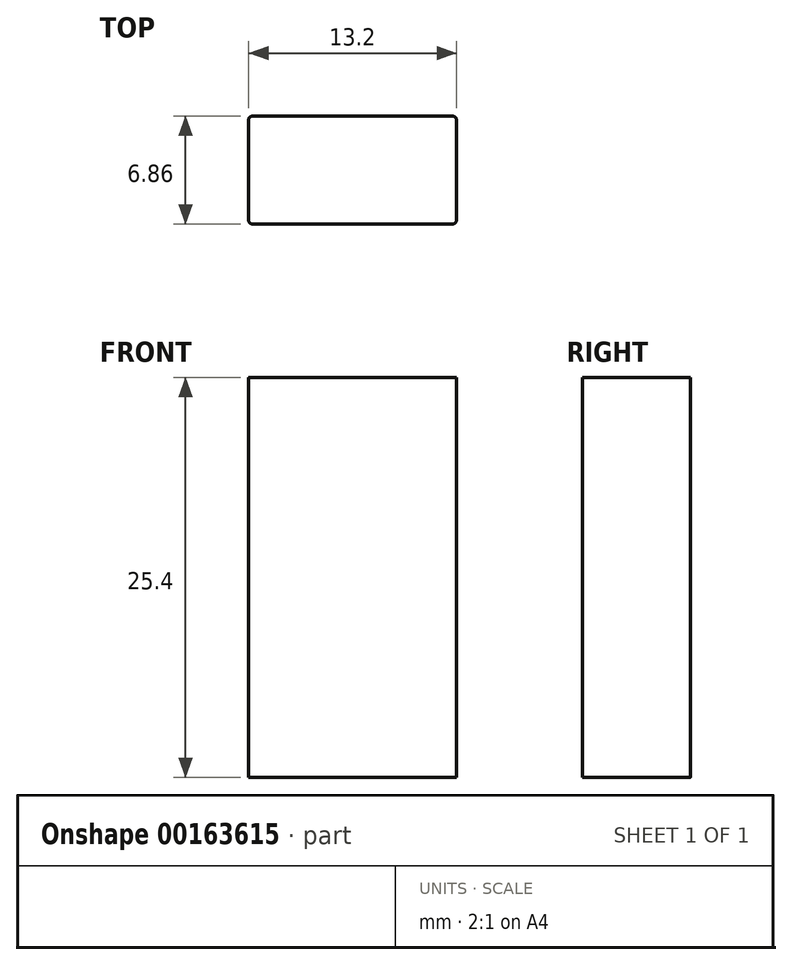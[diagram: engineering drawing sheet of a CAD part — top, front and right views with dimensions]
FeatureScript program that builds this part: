
annotation { "Feature Type Name" : "Feature", "Feature Type Description" : "" }
export const myFeature = defineFeature(function(context is Context, id is Id, definition is map)
    precondition{}
    {
        {
            var Q0;
            Q0=qCreatedBy(makeId("Top.planeOp"),FACE);
            var sketch = newSketch(context, id + "F0", { "sketchPlane" : qUnion([Q0])});
            skLineSegment(sketch, "E0.bottom", {"start": v(6.35, 3.43) * mm, "end": v(-6.35, 3.43) * mm});
            skLineSegment(sketch, "E0.top", {"start": v(6.35, -3.43) * mm, "end": v(-6.35, -3.43) * mm});
            skLineSegment(sketch, "E0.left", {"start": v(6.6, 3.18) * mm, "end": v(6.6, -3.18) * mm});
            skLineSegment(sketch, "E0.right", {"start": v(-6.6, 3.18) * mm, "end": v(-6.6, -3.17) * mm});
            skPoint(sketch, "E0.middle", {"position": v(0, 0) * mm});
            skPoint(sketch, "E1.visualSharp", {"position": v(-6.6, 3.43) * mm});
            skArc(sketch, "E1.filletArc", {"start": v(-6.35, 3.43) * mm, "mid": v(-6.53, 3.35) * mm, "end": v(-6.6, 3.18) * mm});
            skPoint(sketch, "E2.visualSharp", {"position": v(6.6, 3.43) * mm});
            skArc(sketch, "E2.filletArc", {"start": v(6.6, 3.18) * mm, "mid": v(6.53, 3.35) * mm, "end": v(6.35, 3.43) * mm});
            skPoint(sketch, "E3.visualSharp", {"position": v(6.6, -3.43) * mm});
            skArc(sketch, "E3.filletArc", {"start": v(6.35, -3.43) * mm, "mid": v(6.53, -3.35) * mm, "end": v(6.6, -3.18) * mm});
            skPoint(sketch, "E4.visualSharp", {"position": v(-6.6, -3.43) * mm});
            skArc(sketch, "E4.filletArc", {"start": v(-6.6, -3.17) * mm, "mid": v(-6.53, -3.35) * mm, "end": v(-6.35, -3.43) * mm});
            skSolve(sketch);
        }
        {
            var Q0;
            Q0=makeQuery(id+"F0.imprint","IMPRINT",FACE,{"disambiguationData":[TD([[makeQuery(id+"F0.imprint","IMPRINT",EDGE,{"derivedFrom":sQuery(id+"F0.wireOp",EDGE,"E0.bottom")}),1.0]])]});
            extrude(context, id + "F1", {"entities" : qUnion([Q0]), "depth" : 25.4 * mm});
        }
    });
